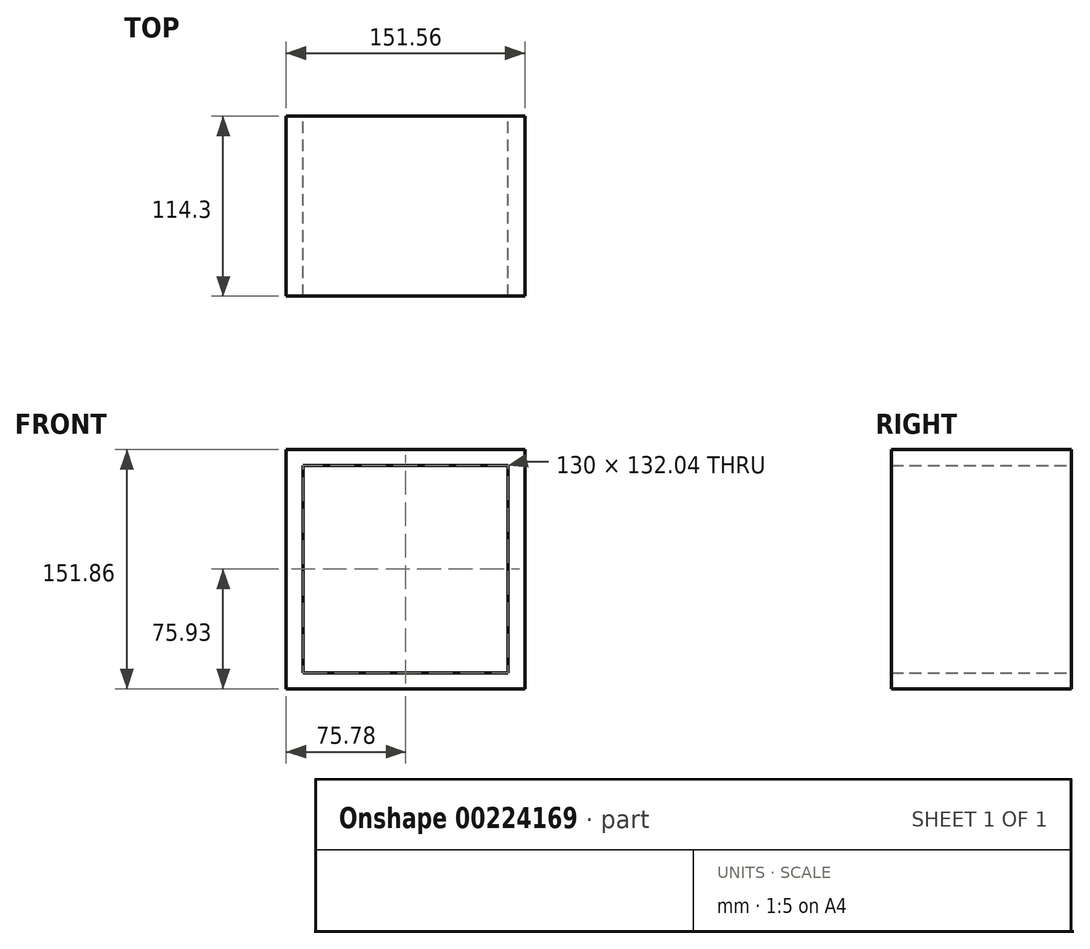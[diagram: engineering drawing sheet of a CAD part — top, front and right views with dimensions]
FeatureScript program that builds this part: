
annotation { "Feature Type Name" : "Feature", "Feature Type Description" : "" }
export const myFeature = defineFeature(function(context is Context, id is Id, definition is map)
    precondition{}
    {
        {
            var Q0;
            Q0=qCreatedBy(makeId("Front.planeOp"),FACE);
            var sketch = newSketch(context, id + "F0", { "sketchPlane" : qUnion([Q0])});
            skLineSegment(sketch, "E0.bottom", {"start": v(-75.78, 75.93) * mm, "end": v(75.78, 75.93) * mm});
            skLineSegment(sketch, "E0.top", {"start": v(-75.78, -75.93) * mm, "end": v(75.78, -75.93) * mm});
            skLineSegment(sketch, "E0.left", {"start": v(-75.78, 75.93) * mm, "end": v(-75.78, -75.93) * mm});
            skLineSegment(sketch, "E0.right", {"start": v(75.78, 75.93) * mm, "end": v(75.78, -75.93) * mm});
            skPoint(sketch, "E0.middle", {"position": v(0, 0) * mm});
            skLineSegment(sketch, "E1.bottom", {"start": v(-65, 66.02) * mm, "end": v(65, 66.02) * mm});
            skLineSegment(sketch, "E1.top", {"start": v(-65, -66.02) * mm, "end": v(65, -66.02) * mm});
            skLineSegment(sketch, "E1.left", {"start": v(-65, 66.02) * mm, "end": v(-65, -66.02) * mm});
            skLineSegment(sketch, "E1.right", {"start": v(65, 66.02) * mm, "end": v(65, -66.02) * mm});
            skSolve(sketch);
        }
        {
            var Q0;
            Q0=makeQuery(id+"F0.imprint","IMPRINT",FACE,{"disambiguationData":[TD([[makeQuery(id+"F0.imprint","IMPRINT",EDGE,{"derivedFrom":sQuery(id+"F0.wireOp",EDGE,"E0.bottom")}),-1.0]])]});
            extrude(context, id + "F1", {"entities" : qUnion([Q0]), "depth" : 114.3 * mm});
        }
    });
